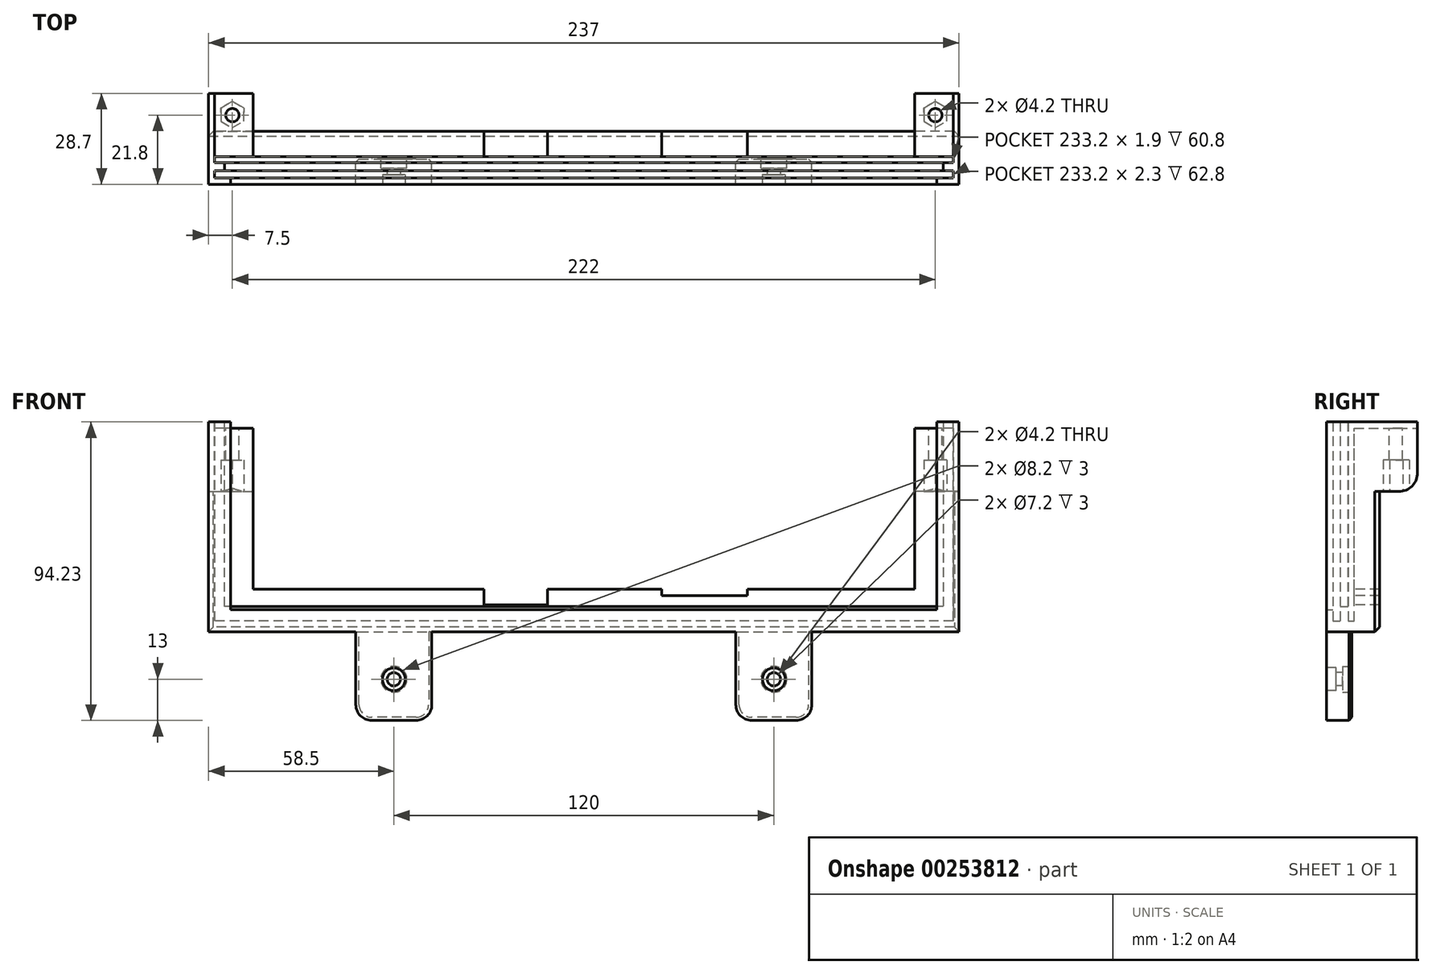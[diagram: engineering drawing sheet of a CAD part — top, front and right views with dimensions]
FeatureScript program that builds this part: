
annotation { "Feature Type Name" : "Feature", "Feature Type Description" : "" }
export const myFeature = defineFeature(function(context is Context, id is Id, definition is map)
    precondition{}
    {
        {
            var Q0;
            Q0=qCreatedBy(makeId("Front.planeOp"),FACE);
            var sketch = newSketch(context, id + "F0", { "sketchPlane" : qUnion([Q0])});
            skLineSegment(sketch, "E0", {"start": v(118.5, 0) * mm, "end": v(118.5, 66.23) * mm});
            skLineSegment(sketch, "E1", {"start": v(118.5, 66.23) * mm, "end": v(104.5, 66.23) * mm});
            skLineSegment(sketch, "E2", {"start": v(104.5, 66.23) * mm, "end": v(104.5, 13.43) * mm});
            skLineSegment(sketch, "E3", {"start": v(104.5, 13.43) * mm, "end": v(-104.5, 13.43) * mm});
            skLineSegment(sketch, "E4", {"start": v(-104.5, 13.43) * mm, "end": v(-104.5, 66.23) * mm});
            skLineSegment(sketch, "E5", {"start": v(-104.5, 66.23) * mm, "end": v(-118.5, 66.23) * mm});
            skLineSegment(sketch, "E6", {"start": v(-118.5, 66.23) * mm, "end": v(-118.5, 0) * mm});
            skLineSegment(sketch, "E7", {"start": v(-118.5, 0) * mm, "end": v(118.5, 0) * mm});
            skSolve(sketch);
        }
        {
            var Q0;
            Q0=makeQuery(id+"F0.imprint","IMPRINT",FACE,{"disambiguationData":[TD([[makeQuery(id+"F0.imprint","IMPRINT",EDGE,{"derivedFrom":sQuery(id+"F0.wireOp",EDGE,"E0")}),1.0]])]});
            extrude(context, id + "F1", {"entities" : qUnion([Q0]), "depth" : 8 * mm, "offsetDistance" : 25 * mm});
        }
        {
            var Q0;
            Q0=makeQuery(id+"F1.opExtrude","CAP_FACE",FACE,{"disambiguationData":[OSD([sQuery(id+"F0.wireOp",EDGE,"E0"),sQuery(id+"F0.wireOp",EDGE,"E1"),sQuery(id+"F0.wireOp",EDGE,"E2"),sQuery(id+"F0.wireOp",EDGE,"E3"),sQuery(id+"F0.wireOp",EDGE,"E4"),sQuery(id+"F0.wireOp",EDGE,"E5"),sQuery(id+"F0.wireOp",EDGE,"E6"),sQuery(id+"F0.wireOp",EDGE,"E7")])],"isStart":false});
            var sketch = newSketch(context, id + "F2", { "sketchPlane" : qUnion([Q0])});
            skLineSegment(sketch, "E8", {"start": v(-118.5, 66.23) * mm, "end": v(-118.5, 0) * mm});
            skLineSegment(sketch, "E9", {"start": v(-118.5, 0) * mm, "end": v(118.5, 0) * mm});
            skLineSegment(sketch, "E10", {"start": v(118.5, 0) * mm, "end": v(118.5, 66.23) * mm});
            skLineSegment(sketch, "E11", {"start": v(118.5, 66.23) * mm, "end": v(116.6, 66.23) * mm});
            skLineSegment(sketch, "E12", {"start": v(116.6, 66.23) * mm, "end": v(116.6, 3.43) * mm});
            skLineSegment(sketch, "E13", {"start": v(116.6, 3.43) * mm, "end": v(-116.6, 3.43) * mm});
            skLineSegment(sketch, "E14", {"start": v(-116.6, 3.43) * mm, "end": v(-116.6, 66.23) * mm});
            skLineSegment(sketch, "E15", {"start": v(-116.6, 66.23) * mm, "end": v(-118.5, 66.23) * mm});
            skSolve(sketch);
        }
        {
            var Q0;
            Q0 = qSketchRegion(id + "F2", true);
            extrude(context, id + "F3", {"entities" : qUnion([Q0]), "operationType" : NewBodyOperationType.ADD, "offsetDistance" : 25 * mm, "depth" : 1.9 * mm});
        }
        {
            var Q0;
            Q0=makeQuery(id+"F3.opExtrude","CAP_FACE",FACE,{"disambiguationData":[OSD([sQuery(id+"F2.wireOp",EDGE,"E8"),sQuery(id+"F2.wireOp",EDGE,"E9"),sQuery(id+"F2.wireOp",EDGE,"E10"),sQuery(id+"F2.wireOp",EDGE,"E11"),sQuery(id+"F2.wireOp",EDGE,"E12"),sQuery(id+"F2.wireOp",EDGE,"E13"),sQuery(id+"F2.wireOp",EDGE,"E14"),sQuery(id+"F2.wireOp",EDGE,"E15")])],"isStart":false});
            var sketch = newSketch(context, id + "F4", { "sketchPlane" : qUnion([Q0])});
            skLineSegment(sketch, "E16", {"start": v(-118.5, 66.23) * mm, "end": v(-118.5, 0) * mm});
            skLineSegment(sketch, "E17", {"start": v(-118.5, 0) * mm, "end": v(118.5, 0) * mm});
            skLineSegment(sketch, "E18", {"start": v(118.5, 0) * mm, "end": v(118.5, 66.23) * mm});
            skLineSegment(sketch, "E19", {"start": v(118.5, 66.23) * mm, "end": v(113.5, 66.23) * mm});
            skLineSegment(sketch, "E20", {"start": v(-113.5, 8) * mm, "end": v(-113.5, 66.23) * mm});
            skLineSegment(sketch, "E21", {"start": v(-113.5, 66.23) * mm, "end": v(-118.5, 66.23) * mm});
            skLineSegment(sketch, "E22", {"start": v(113.5, 66.23) * mm, "end": v(113.5, 8) * mm});
            skLineSegment(sketch, "E23", {"start": v(113.5, 8) * mm, "end": v(-113.5, 8) * mm});
            skSolve(sketch);
        }
        {
            var Q0;
            Q0 = qSketchRegion(id + "F4", true);
            extrude(context, id + "F5", {"entities" : qUnion([Q0]), "operationType" : NewBodyOperationType.ADD, "offsetDistance" : 25 * mm, "depth" : 2.5 * mm});
        }
        {
            var Q0;
            Q0=makeQuery(id+"F5.opExtrude","CAP_FACE",FACE,{"disambiguationData":[OSD([sQuery(id+"F4.wireOp",EDGE,"E16"),sQuery(id+"F4.wireOp",EDGE,"E17"),sQuery(id+"F4.wireOp",EDGE,"E18"),sQuery(id+"F4.wireOp",EDGE,"E19"),sQuery(id+"F4.wireOp",EDGE,"Wqc7Pmu5-h7pA-NfiT-lCzg-tGP6uvwJ4WZ4"),sQuery(id+"F4.wireOp",EDGE,"H4PolKqh-P5Vf-ZCvA-0sDl-Pb70Bhz4lyF4"),sQuery(id+"F4.wireOp",EDGE,"E20"),sQuery(id+"F4.wireOp",EDGE,"E21")])],"isStart":false});
            var sketch = newSketch(context, id + "F6", { "sketchPlane" : qUnion([Q0])});
            skLineSegment(sketch, "E24", {"start": v(-118.5, 66.23) * mm, "end": v(-116.6, 66.23) * mm});
            skLineSegment(sketch, "E25", {"start": v(-116.6, 66.23) * mm, "end": v(-116.6, 3.43) * mm});
            skLineSegment(sketch, "E26", {"start": v(-116.6, 3.43) * mm, "end": v(116.6, 3.43) * mm});
            skLineSegment(sketch, "E27", {"start": v(116.6, 3.43) * mm, "end": v(116.6, 66.23) * mm});
            skLineSegment(sketch, "E28", {"start": v(116.6, 66.23) * mm, "end": v(118.5, 66.23) * mm});
            skLineSegment(sketch, "E29", {"start": v(118.5, 66.23) * mm, "end": v(118.5, 0) * mm});
            skLineSegment(sketch, "E30", {"start": v(118.5, 0) * mm, "end": v(-118.5, 0) * mm});
            skLineSegment(sketch, "E31", {"start": v(-118.5, 0) * mm, "end": v(-118.5, 66.23) * mm});
            skSolve(sketch);
        }
        {
            var Q0;
            Q0 = qSketchRegion(id + "F6", true);
            extrude(context, id + "F7", {"entities" : qUnion([Q0]), "operationType" : NewBodyOperationType.ADD, "offsetDistance" : 25 * mm, "depth" : 2.3 * mm});
        }
        {
            var Q0;
            Q0=makeQuery(id+"F7.opExtrude","CAP_FACE",FACE,{"disambiguationData":[OSD([sQuery(id+"F6.wireOp",EDGE,"E24"),sQuery(id+"F6.wireOp",EDGE,"E25"),sQuery(id+"F6.wireOp",EDGE,"E26"),sQuery(id+"F6.wireOp",EDGE,"E27"),sQuery(id+"F6.wireOp",EDGE,"E28"),sQuery(id+"F6.wireOp",EDGE,"E29"),sQuery(id+"F6.wireOp",EDGE,"E30"),sQuery(id+"F6.wireOp",EDGE,"E31")])],"isStart":false});
            var sketch = newSketch(context, id + "F8", { "sketchPlane" : qUnion([Q0])});
            skLineSegment(sketch, "E32", {"start": v(-118.5, 66.23) * mm, "end": v(-118.5, 0) * mm});
            skLineSegment(sketch, "E33", {"start": v(-118.5, 0) * mm, "end": v(118.5, 0) * mm});
            skLineSegment(sketch, "E34", {"start": v(118.5, 0) * mm, "end": v(118.5, 66.23) * mm});
            skLineSegment(sketch, "E35", {"start": v(118.5, 66.23) * mm, "end": v(111.5, 66.23) * mm});
            skLineSegment(sketch, "E36", {"start": v(111.5, 66.23) * mm, "end": v(111.5, 7) * mm});
            skLineSegment(sketch, "E37", {"start": v(111.5, 7) * mm, "end": v(-111.5, 7) * mm});
            skLineSegment(sketch, "E38", {"start": v(-111.5, 7) * mm, "end": v(-111.5, 66.23) * mm});
            skLineSegment(sketch, "E39", {"start": v(-111.5, 66.23) * mm, "end": v(-118.5, 66.23) * mm});
            skSolve(sketch);
        }
        {
            var Q0;
            Q0=makeQuery(id+"F1.opExtrude","CAP_FACE",FACE,{"disambiguationData":[OSD([sQuery(id+"F0.wireOp",EDGE,"E0"),sQuery(id+"F0.wireOp",EDGE,"E1"),sQuery(id+"F0.wireOp",EDGE,"E2"),sQuery(id+"F0.wireOp",EDGE,"E3"),sQuery(id+"F0.wireOp",EDGE,"E4"),sQuery(id+"F0.wireOp",EDGE,"E5"),sQuery(id+"F0.wireOp",EDGE,"E6"),sQuery(id+"F0.wireOp",EDGE,"E7")])],"isStart":true});
            var sketch = newSketch(context, id + "F9", { "sketchPlane" : qUnion([Q0])});
            skLineSegment(sketch, "E40.bottom", {"start": v(118.5, 66.23) * mm, "end": v(104.5, 66.23) * mm});
            skLineSegment(sketch, "E40.top", {"start": v(118.5, 44.23) * mm, "end": v(104.5, 44.23) * mm});
            skLineSegment(sketch, "E40.left", {"start": v(118.5, 66.23) * mm, "end": v(118.5, 44.23) * mm});
            skLineSegment(sketch, "E40.right", {"start": v(104.5, 66.23) * mm, "end": v(104.5, 44.23) * mm});
            skLineSegment(sketch, "E41.bottom", {"start": v(-118.5, 66.23) * mm, "end": v(-104.5, 66.23) * mm});
            skLineSegment(sketch, "E41.top", {"start": v(-118.5, 44.23) * mm, "end": v(-104.5, 44.23) * mm});
            skLineSegment(sketch, "E41.left", {"start": v(-118.5, 66.23) * mm, "end": v(-118.5, 44.23) * mm});
            skLineSegment(sketch, "E41.right", {"start": v(-104.5, 66.23) * mm, "end": v(-104.5, 44.23) * mm});
            skSolve(sketch);
        }
        {
            var Q0;
            Q0 = qSketchRegion(id + "F9", true);
            extrude(context, id + "F10", {"entities" : qUnion([Q0]), "operationType" : NewBodyOperationType.ADD, "depth" : 12 * mm, "offsetDistance" : 25 * mm});
        }
        {
            var Q0;
            Q0 = qSketchRegion(id + "F8", true);
            extrude(context, id + "F11", {"entities" : qUnion([Q0]), "operationType" : NewBodyOperationType.ADD, "depth" : 2 * mm});
        }
        {
            var Q0;
            Q0=makeQuery(id+"F11.boolean.opBoolean","MERGE",FACE,{"derivedFrom":[makeQuery(id+"F7.boolean.opBoolean","MERGE",FACE,{"derivedFrom":[makeQuery(id+"F5.boolean.opBoolean","MERGE",FACE,{"derivedFrom":[makeQuery(id+"F3.boolean.opBoolean","MERGE",FACE,{"derivedFrom":[makeQuery(id+"F1.opExtrude","SWEPT_FACE",FACE,{"disambiguationData":[OSD([sQuery(id+"F0.wireOp",EDGE,"E5")])]}),makeQuery(id+"F3.opExtrude","SWEPT_FACE",FACE,{"disambiguationData":[OSD([sQuery(id+"F2.wireOp",EDGE,"E15")])]})]}),makeQuery(id+"F5.opExtrude","SWEPT_FACE",FACE,{"disambiguationData":[OSD([sQuery(id+"F4.wireOp",EDGE,"E21")])]})]}),makeQuery(id+"F7.opExtrude","SWEPT_FACE",FACE,{"disambiguationData":[OSD([sQuery(id+"F6.wireOp",EDGE,"E24")])]})]}),makeQuery(id+"F11.opExtrude","SWEPT_FACE",FACE,{"disambiguationData":[OSD([sQuery(id+"F8.wireOp",EDGE,"E39")])]})]});
            var sketch = newSketch(context, id + "F12", { "sketchPlane" : qUnion([Q0])});
            skLineSegment(sketch, "E42.bottom", {"start": v(-116.6, -8) * mm, "end": v(-104.5, -8) * mm});
            skLineSegment(sketch, "E42.top", {"start": v(-116.6, 12) * mm, "end": v(-104.5, 12) * mm});
            skLineSegment(sketch, "E42.left", {"start": v(-116.6, -8) * mm, "end": v(-116.6, 12) * mm});
            skLineSegment(sketch, "E42.right", {"start": v(-104.5, -8) * mm, "end": v(-104.5, 12) * mm});
            skSolve(sketch);
        }
        {
            var Q0;
            Q0=makeQuery(id+"F11.boolean.opBoolean","MERGE",FACE,{"derivedFrom":[makeQuery(id+"F7.boolean.opBoolean","MERGE",FACE,{"derivedFrom":[makeQuery(id+"F5.boolean.opBoolean","MERGE",FACE,{"derivedFrom":[makeQuery(id+"F3.boolean.opBoolean","MERGE",FACE,{"derivedFrom":[makeQuery(id+"F1.opExtrude","SWEPT_FACE",FACE,{"disambiguationData":[OSD([sQuery(id+"F0.wireOp",EDGE,"E1")])]}),makeQuery(id+"F3.opExtrude","SWEPT_FACE",FACE,{"disambiguationData":[OSD([sQuery(id+"F2.wireOp",EDGE,"E11")])]})]}),makeQuery(id+"F5.opExtrude","SWEPT_FACE",FACE,{"disambiguationData":[OSD([sQuery(id+"F4.wireOp",EDGE,"E19")])]})]}),makeQuery(id+"F7.opExtrude","SWEPT_FACE",FACE,{"disambiguationData":[OSD([sQuery(id+"F6.wireOp",EDGE,"E28")])]})]}),makeQuery(id+"F11.opExtrude","SWEPT_FACE",FACE,{"disambiguationData":[OSD([sQuery(id+"F8.wireOp",EDGE,"E35")])]})]});
            var sketch = newSketch(context, id + "F13", { "sketchPlane" : qUnion([Q0])});
            skLineSegment(sketch, "E43.bottom", {"start": v(116.6, -8) * mm, "end": v(104.5, -8) * mm});
            skLineSegment(sketch, "E43.top", {"start": v(116.6, 12) * mm, "end": v(104.5, 12) * mm});
            skLineSegment(sketch, "E43.left", {"start": v(116.6, -8) * mm, "end": v(116.6, 12) * mm});
            skLineSegment(sketch, "E43.right", {"start": v(104.5, -8) * mm, "end": v(104.5, 12) * mm});
            skSolve(sketch);
        }
        {
            var Q0;
            Q0 = qSketchRegion(id + "F12", true);
            var Q1;
            Q1 = qSketchRegion(id + "F13", true);
            extrude(context, id + "F14", {"entities" : qUnion([Q0, Q1]), "operationType" : NewBodyOperationType.REMOVE, "oppositeDirection" : true, "depth" : 2 * mm});
        }
        {
            var Q0;
            Q0=makeQuery(id+"F10.opExtrude","SWEPT_FACE",FACE,{"disambiguationData":[OSD([sQuery(id+"F9.wireOp",EDGE,"E41.top")])]});
            var sketch = newSketch(context, id + "F15", { "sketchPlane" : qUnion([Q0])});
            skCircle(sketch, "E44.cCircle", {"center": v(111, -5.3) * mm, "radius": 3.6 * mm, "construction": true});
            skLineSegment(sketch, "E44.0", {"start": v(107.4, -3.22) * mm, "end": v(111, -1.14) * mm});
            skLineSegment(sketch, "E44.1", {"start": v(111, -1.14) * mm, "end": v(114.6, -3.22) * mm});
            skLineSegment(sketch, "E44.2", {"start": v(114.6, -3.22) * mm, "end": v(114.6, -7.38) * mm});
            skLineSegment(sketch, "E44.3", {"start": v(114.6, -7.38) * mm, "end": v(111, -9.46) * mm});
            skLineSegment(sketch, "E44.4", {"start": v(111, -9.46) * mm, "end": v(107.4, -7.38) * mm});
            skLineSegment(sketch, "E44.5", {"start": v(107.4, -7.38) * mm, "end": v(107.4, -3.22) * mm});
            skPoint(sketch, "E44.0.midPoint", {"position": v(109.2, -2.18) * mm});
            skSolve(sketch);
        }
        {
            var Q0;
            Q0=makeQuery(id+"F10.opExtrude","SWEPT_FACE",FACE,{"disambiguationData":[OSD([sQuery(id+"F9.wireOp",EDGE,"E40.top")])]});
            var sketch = newSketch(context, id + "F16", { "sketchPlane" : qUnion([Q0])});
            skCircle(sketch, "E45.cCircle", {"center": v(-111, -5.3) * mm, "radius": 3.6 * mm, "construction": true});
            skLineSegment(sketch, "E45.0", {"start": v(-107.4, -3.22) * mm, "end": v(-107.4, -7.38) * mm});
            skLineSegment(sketch, "E45.1", {"start": v(-107.4, -7.38) * mm, "end": v(-111, -9.46) * mm});
            skLineSegment(sketch, "E45.2", {"start": v(-111, -9.46) * mm, "end": v(-114.6, -7.38) * mm});
            skLineSegment(sketch, "E45.3", {"start": v(-114.6, -7.38) * mm, "end": v(-114.6, -3.22) * mm});
            skLineSegment(sketch, "E45.4", {"start": v(-114.6, -3.22) * mm, "end": v(-111, -1.14) * mm});
            skLineSegment(sketch, "E45.5", {"start": v(-111, -1.14) * mm, "end": v(-107.4, -3.22) * mm});
            skPoint(sketch, "E45.0.midPoint", {"position": v(-107.4, -5.3) * mm});
            skSolve(sketch);
        }
        {
            var Q0;
            {var subQ0=sQuery(id+"F9.wireOp",EDGE,"E40.top");Q0=makeQuery(id+"F10.boolean.opBoolean","SPLIT",EDGE,{"disambiguationData":[topologyDisambiguationEdgeConnected([makeQuery(id+"F1.opExtrude","CAP_FACE",FACE,{"disambiguationData":[OSD([sQuery(id+"F0.wireOp",EDGE,"E0"),sQuery(id+"F0.wireOp",EDGE,"E1"),sQuery(id+"F0.wireOp",EDGE,"E2"),sQuery(id+"F0.wireOp",EDGE,"E3"),sQuery(id+"F0.wireOp",EDGE,"E4"),sQuery(id+"F0.wireOp",EDGE,"E5"),sQuery(id+"F0.wireOp",EDGE,"E6"),sQuery(id+"F0.wireOp",EDGE,"E7")])],"isStart":true})])],"derivedFrom":makeQuery(id+"F10.opExtrude","CAP_EDGE",EDGE,{"disambiguationData":[OSD([subQ0])],"isStart":true})});}
            var Q1;
            Q1=makeQuery(id+"F10.opExtrude","CAP_EDGE",EDGE,{"disambiguationData":[OSD([sQuery(id+"F9.wireOp",EDGE,"E40.top")])],"isStart":false});
            var Q2;
            Q2=makeQuery(id+"F10.opExtrude","CAP_EDGE",EDGE,{"disambiguationData":[OSD([sQuery(id+"F9.wireOp",EDGE,"zH6vjrLi-htQf-ZEOU-owel-cehFYXmzGVBA.top")])],"isStart":true});
            var Q3;
            Q3=makeQuery(id+"F10.opExtrude","CAP_EDGE",EDGE,{"disambiguationData":[OSD([sQuery(id+"F9.wireOp",EDGE,"zH6vjrLi-htQf-ZEOU-owel-cehFYXmzGVBA.bottom")])],"isStart":false});
            fillet(context, id + "F17", {"entities" : qUnion([Q0, Q1, Q2, Q3]), "radius" : 6 * mm, "tangentPropagation" : true, "allowEdgeOverflow" : false});
        }
        {
            var Q0;
            {var subQ0=sQuery(id+"F9.wireOp",EDGE,"E41.top");Q0=makeQuery(id+"F10.boolean.opBoolean","SPLIT",EDGE,{"disambiguationData":[topologyDisambiguationEdgeConnected([makeQuery(id+"F1.opExtrude","CAP_FACE",FACE,{"disambiguationData":[OSD([sQuery(id+"F0.wireOp",EDGE,"E0"),sQuery(id+"F0.wireOp",EDGE,"E1"),sQuery(id+"F0.wireOp",EDGE,"E2"),sQuery(id+"F0.wireOp",EDGE,"E3"),sQuery(id+"F0.wireOp",EDGE,"E4"),sQuery(id+"F0.wireOp",EDGE,"E5"),sQuery(id+"F0.wireOp",EDGE,"E6"),sQuery(id+"F0.wireOp",EDGE,"E7")])],"isStart":true})])],"derivedFrom":makeQuery(id+"F10.opExtrude","CAP_EDGE",EDGE,{"disambiguationData":[OSD([subQ0])],"isStart":true})});}
            var Q1;
            Q1=makeQuery(id+"F10.opExtrude","CAP_EDGE",EDGE,{"disambiguationData":[OSD([sQuery(id+"F9.wireOp",EDGE,"E41.top")])],"isStart":false});
            var Q2;
            Q2=makeQuery(id+"F10.opExtrude","CAP_EDGE",EDGE,{"disambiguationData":[OSD([sQuery(id+"F9.wireOp",EDGE,"rV4yrqaR-FLz1-uUMA-ZUjG-8FGM3lznCrda.top")])],"isStart":true});
            var Q3;
            Q3=makeQuery(id+"F10.opExtrude","CAP_EDGE",EDGE,{"disambiguationData":[OSD([sQuery(id+"F9.wireOp",EDGE,"rV4yrqaR-FLz1-uUMA-ZUjG-8FGM3lznCrda.bottom")])],"isStart":false});
            fillet(context, id + "F18", {"entities" : qUnion([Q0, Q1, Q2, Q3]), "radius" : 6 * mm, "tangentPropagation" : true, "allowEdgeOverflow" : false});
        }
        {
            var Q0;
            Q0 = qSketchRegion(id + "F15", true);
            var Q1;
            Q1 = qSketchRegion(id + "F16", true);
            extrude(context, id + "F19", {"entities" : qUnion([Q0, Q1]), "operationType" : NewBodyOperationType.REMOVE, "oppositeDirection" : true, "depth" : 10 * mm});
        }
        {
            var Q0;
            Q0 = qSketchRegion(id + "F15", true);
            var Q1;
            Q1 = qSketchRegion(id + "F16", true);
            extrude(context, id + "F20", {"entities" : qUnion([Q0, Q1]), "operationType" : NewBodyOperationType.REMOVE, "depth" : 25 * mm});
        }
        {
            var Q0;
            Q0=makeQuery(id+"F14.boolean.opBoolean","COPY",FACE,{"derivedFrom":makeQuery(id+"F14.opExtrude","CAP_FACE",FACE,{"disambiguationData":[OSD([sQuery(id+"F12.wireOp",EDGE,"E42.bottom"),sQuery(id+"F12.wireOp",EDGE,"E42.top"),sQuery(id+"F12.wireOp",EDGE,"E42.left"),sQuery(id+"F12.wireOp",EDGE,"E42.right")])],"isStart":false})});
            var sketch = newSketch(context, id + "F21", { "sketchPlane" : qUnion([Q0])});
            skCircle(sketch, "E46", {"center": v(-111, 5.1) * mm, "radius": 2.1 * mm});
            skSolve(sketch);
        }
        {
            var Q0;
            Q0=makeQuery(id+"F14.boolean.opBoolean","COPY",FACE,{"derivedFrom":makeQuery(id+"F14.opExtrude","CAP_FACE",FACE,{"disambiguationData":[OSD([sQuery(id+"F13.wireOp",EDGE,"E43.bottom"),sQuery(id+"F13.wireOp",EDGE,"E43.top"),sQuery(id+"F13.wireOp",EDGE,"E43.left"),sQuery(id+"F13.wireOp",EDGE,"E43.right")])],"isStart":false})});
            var sketch = newSketch(context, id + "F22", { "sketchPlane" : qUnion([Q0])});
            skCircle(sketch, "E47", {"center": v(111, 5.1) * mm, "radius": 2.1 * mm});
            skSolve(sketch);
        }
        {
            var Q0;
            Q0 = qSketchRegion(id + "F22", true);
            var Q1;
            Q1 = qSketchRegion(id + "F21", true);
            extrude(context, id + "F23", {"entities" : qUnion([Q0, Q1]), "operationType" : NewBodyOperationType.REMOVE, "endBound" : BoundingType.UP_TO_NEXT, "oppositeDirection" : true, "depth" : 25 * mm, "offsetDistance" : 25 * mm});
        }
        {
            var Q0;
            Q0=makeQuery(id+"F1.opExtrude","CAP_EDGE",EDGE,{"disambiguationData":[OSD([sQuery(id+"F0.wireOp",EDGE,"E0")])],"isStart":true});
            var Q1;
            Q1=makeQuery(id+"F17.opFillet","BLEND_EDGE",EDGE,{"blendedFrom":[makeQuery(id+"F10.boolean.opBoolean","COPY",EDGE,{"derivedFrom":makeQuery(id+"F10.opExtrude","CAP_EDGE",EDGE,{"disambiguationData":[OSD([sQuery(id+"F9.wireOp",EDGE,"GcGkKbpC-YmWN-ICau-n4Ke-VAg4k9SfYREq")])],"isStart":true})}),makeQuery(id+"F11.boolean.opBoolean","MERGE",FACE,{"derivedFrom":[makeQuery(id+"F7.boolean.opBoolean","MERGE",FACE,{"derivedFrom":[makeQuery(id+"F5.boolean.opBoolean","MERGE",FACE,{"derivedFrom":[makeQuery(id+"F3.boolean.opBoolean","MERGE",FACE,{"derivedFrom":[makeQuery(id+"F1.opExtrude","SWEPT_FACE",FACE,{"disambiguationData":[OSD([sQuery(id+"F0.wireOp",EDGE,"E0")])]}),makeQuery(id+"F3.opExtrude","SWEPT_FACE",FACE,{"disambiguationData":[OSD([sQuery(id+"F2.wireOp",EDGE,"E10")])]})]}),makeQuery(id+"F5.opExtrude","SWEPT_FACE",FACE,{"disambiguationData":[OSD([sQuery(id+"F4.wireOp",EDGE,"E18")])]})]}),makeQuery(id+"F7.opExtrude","SWEPT_FACE",FACE,{"disambiguationData":[OSD([sQuery(id+"F6.wireOp",EDGE,"E29")])]})]}),makeQuery(id+"F11.opExtrude","SWEPT_FACE",FACE,{"disambiguationData":[OSD([sQuery(id+"F8.wireOp",EDGE,"E34")])]})]})],"blendedInto":[makeQuery(id+"F11.boolean.opBoolean","MERGE",FACE,{"derivedFrom":[makeQuery(id+"F7.boolean.opBoolean","MERGE",FACE,{"derivedFrom":[makeQuery(id+"F5.boolean.opBoolean","MERGE",FACE,{"derivedFrom":[makeQuery(id+"F3.boolean.opBoolean","MERGE",FACE,{"derivedFrom":[makeQuery(id+"F1.opExtrude","SWEPT_FACE",FACE,{"disambiguationData":[OSD([sQuery(id+"F0.wireOp",EDGE,"E0")])]}),makeQuery(id+"F3.opExtrude","SWEPT_FACE",FACE,{"disambiguationData":[OSD([sQuery(id+"F2.wireOp",EDGE,"E10")])]})]}),makeQuery(id+"F5.opExtrude","SWEPT_FACE",FACE,{"disambiguationData":[OSD([sQuery(id+"F4.wireOp",EDGE,"E18")])]})]}),makeQuery(id+"F7.opExtrude","SWEPT_FACE",FACE,{"disambiguationData":[OSD([sQuery(id+"F6.wireOp",EDGE,"E29")])]})]}),makeQuery(id+"F11.opExtrude","SWEPT_FACE",FACE,{"disambiguationData":[OSD([sQuery(id+"F8.wireOp",EDGE,"E34")])]})]})]});
            var Q2;
            Q2=makeQuery(id+"F17.opFillet","BLEND_EDGE",EDGE,{"blendedFrom":[makeQuery(id+"F10.boolean.opBoolean","COPY",EDGE,{"derivedFrom":makeQuery(id+"F10.opExtrude","CAP_EDGE",EDGE,{"disambiguationData":[OSD([sQuery(id+"F9.wireOp",EDGE,"GcGkKbpC-YmWN-ICau-n4Ke-VAg4k9SfYREq")])],"isStart":false})}),makeQuery(id+"F11.boolean.opBoolean","MERGE",FACE,{"derivedFrom":[makeQuery(id+"F7.boolean.opBoolean","MERGE",FACE,{"derivedFrom":[makeQuery(id+"F5.boolean.opBoolean","MERGE",FACE,{"derivedFrom":[makeQuery(id+"F3.boolean.opBoolean","MERGE",FACE,{"derivedFrom":[makeQuery(id+"F1.opExtrude","SWEPT_FACE",FACE,{"disambiguationData":[OSD([sQuery(id+"F0.wireOp",EDGE,"E0")])]}),makeQuery(id+"F3.opExtrude","SWEPT_FACE",FACE,{"disambiguationData":[OSD([sQuery(id+"F2.wireOp",EDGE,"E10")])]})]}),makeQuery(id+"F5.opExtrude","SWEPT_FACE",FACE,{"disambiguationData":[OSD([sQuery(id+"F4.wireOp",EDGE,"E18")])]})]}),makeQuery(id+"F7.opExtrude","SWEPT_FACE",FACE,{"disambiguationData":[OSD([sQuery(id+"F6.wireOp",EDGE,"E29")])]})]}),makeQuery(id+"F11.opExtrude","SWEPT_FACE",FACE,{"disambiguationData":[OSD([sQuery(id+"F8.wireOp",EDGE,"E34")])]})]})],"blendedInto":[makeQuery(id+"F11.boolean.opBoolean","MERGE",FACE,{"derivedFrom":[makeQuery(id+"F7.boolean.opBoolean","MERGE",FACE,{"derivedFrom":[makeQuery(id+"F5.boolean.opBoolean","MERGE",FACE,{"derivedFrom":[makeQuery(id+"F3.boolean.opBoolean","MERGE",FACE,{"derivedFrom":[makeQuery(id+"F1.opExtrude","SWEPT_FACE",FACE,{"disambiguationData":[OSD([sQuery(id+"F0.wireOp",EDGE,"E0")])]}),makeQuery(id+"F3.opExtrude","SWEPT_FACE",FACE,{"disambiguationData":[OSD([sQuery(id+"F2.wireOp",EDGE,"E10")])]})]}),makeQuery(id+"F5.opExtrude","SWEPT_FACE",FACE,{"disambiguationData":[OSD([sQuery(id+"F4.wireOp",EDGE,"E18")])]})]}),makeQuery(id+"F7.opExtrude","SWEPT_FACE",FACE,{"disambiguationData":[OSD([sQuery(id+"F6.wireOp",EDGE,"E29")])]})]}),makeQuery(id+"F11.opExtrude","SWEPT_FACE",FACE,{"disambiguationData":[OSD([sQuery(id+"F8.wireOp",EDGE,"E34")])]})]})]});
            var Q3;
            Q3=makeQuery(id+"F10.boolean.opBoolean","COPY",EDGE,{"derivedFrom":makeQuery(id+"F10.opExtrude","CAP_EDGE",EDGE,{"disambiguationData":[OSD([sQuery(id+"F9.wireOp",EDGE,"H9YxvoyA-mwdu-Ozs1-Mgqu-f7LAvOGyu2lw")])],"isStart":false})});
            var Q4;
            Q4=makeQuery(id+"F10.boolean.opBoolean","COPY",EDGE,{"derivedFrom":makeQuery(id+"F10.opExtrude","CAP_EDGE",EDGE,{"disambiguationData":[OSD([sQuery(id+"F9.wireOp",EDGE,"rf6zfMRu-Qe2T-Zb9I-k2tc-n19xOsOlgDaL")])],"isStart":false})});
            var Q5;
            Q5=makeQuery(id+"F10.boolean.opBoolean","COPY",EDGE,{"derivedFrom":makeQuery(id+"F10.opExtrude","CAP_EDGE",EDGE,{"disambiguationData":[OSD([sQuery(id+"F9.wireOp",EDGE,"47vZZXop-T4Wf-DfnT-CCxK-A6Yf87ua8k3M")])],"isStart":false})});
            var Q6;
            Q6=makeQuery(id+"F18.opFillet","BLEND_EDGE",EDGE,{"blendedFrom":[makeQuery(id+"F10.boolean.opBoolean","COPY",EDGE,{"derivedFrom":makeQuery(id+"F10.opExtrude","CAP_EDGE",EDGE,{"disambiguationData":[OSD([sQuery(id+"F9.wireOp",EDGE,"PPJEcUq0-yMRA-Zqzy-vXhF-8VfT6uxw4NmP")])],"isStart":false})}),makeQuery(id+"F11.boolean.opBoolean","MERGE",FACE,{"derivedFrom":[makeQuery(id+"F7.boolean.opBoolean","MERGE",FACE,{"derivedFrom":[makeQuery(id+"F5.boolean.opBoolean","MERGE",FACE,{"derivedFrom":[makeQuery(id+"F3.boolean.opBoolean","MERGE",FACE,{"derivedFrom":[makeQuery(id+"F1.opExtrude","SWEPT_FACE",FACE,{"disambiguationData":[OSD([sQuery(id+"F0.wireOp",EDGE,"E6")])]}),makeQuery(id+"F3.opExtrude","SWEPT_FACE",FACE,{"disambiguationData":[OSD([sQuery(id+"F2.wireOp",EDGE,"E8")])]})]}),makeQuery(id+"F5.opExtrude","SWEPT_FACE",FACE,{"disambiguationData":[OSD([sQuery(id+"F4.wireOp",EDGE,"E16")])]})]}),makeQuery(id+"F7.opExtrude","SWEPT_FACE",FACE,{"disambiguationData":[OSD([sQuery(id+"F6.wireOp",EDGE,"E31")])]})]}),makeQuery(id+"F11.opExtrude","SWEPT_FACE",FACE,{"disambiguationData":[OSD([sQuery(id+"F8.wireOp",EDGE,"E32")])]})]})],"blendedInto":[makeQuery(id+"F11.boolean.opBoolean","MERGE",FACE,{"derivedFrom":[makeQuery(id+"F7.boolean.opBoolean","MERGE",FACE,{"derivedFrom":[makeQuery(id+"F5.boolean.opBoolean","MERGE",FACE,{"derivedFrom":[makeQuery(id+"F3.boolean.opBoolean","MERGE",FACE,{"derivedFrom":[makeQuery(id+"F1.opExtrude","SWEPT_FACE",FACE,{"disambiguationData":[OSD([sQuery(id+"F0.wireOp",EDGE,"E6")])]}),makeQuery(id+"F3.opExtrude","SWEPT_FACE",FACE,{"disambiguationData":[OSD([sQuery(id+"F2.wireOp",EDGE,"E8")])]})]}),makeQuery(id+"F5.opExtrude","SWEPT_FACE",FACE,{"disambiguationData":[OSD([sQuery(id+"F4.wireOp",EDGE,"E16")])]})]}),makeQuery(id+"F7.opExtrude","SWEPT_FACE",FACE,{"disambiguationData":[OSD([sQuery(id+"F6.wireOp",EDGE,"E31")])]})]}),makeQuery(id+"F11.opExtrude","SWEPT_FACE",FACE,{"disambiguationData":[OSD([sQuery(id+"F8.wireOp",EDGE,"E32")])]})]})]});
            var Q7;
            Q7=makeQuery(id+"F18.opFillet","BLEND_EDGE",EDGE,{"blendedFrom":[makeQuery(id+"F10.boolean.opBoolean","COPY",EDGE,{"derivedFrom":makeQuery(id+"F10.opExtrude","CAP_EDGE",EDGE,{"disambiguationData":[OSD([sQuery(id+"F9.wireOp",EDGE,"PPJEcUq0-yMRA-Zqzy-vXhF-8VfT6uxw4NmP")])],"isStart":true})}),makeQuery(id+"F11.boolean.opBoolean","MERGE",FACE,{"derivedFrom":[makeQuery(id+"F7.boolean.opBoolean","MERGE",FACE,{"derivedFrom":[makeQuery(id+"F5.boolean.opBoolean","MERGE",FACE,{"derivedFrom":[makeQuery(id+"F3.boolean.opBoolean","MERGE",FACE,{"derivedFrom":[makeQuery(id+"F1.opExtrude","SWEPT_FACE",FACE,{"disambiguationData":[OSD([sQuery(id+"F0.wireOp",EDGE,"E6")])]}),makeQuery(id+"F3.opExtrude","SWEPT_FACE",FACE,{"disambiguationData":[OSD([sQuery(id+"F2.wireOp",EDGE,"E8")])]})]}),makeQuery(id+"F5.opExtrude","SWEPT_FACE",FACE,{"disambiguationData":[OSD([sQuery(id+"F4.wireOp",EDGE,"E16")])]})]}),makeQuery(id+"F7.opExtrude","SWEPT_FACE",FACE,{"disambiguationData":[OSD([sQuery(id+"F6.wireOp",EDGE,"E31")])]})]}),makeQuery(id+"F11.opExtrude","SWEPT_FACE",FACE,{"disambiguationData":[OSD([sQuery(id+"F8.wireOp",EDGE,"E32")])]})]})],"blendedInto":[makeQuery(id+"F11.boolean.opBoolean","MERGE",FACE,{"derivedFrom":[makeQuery(id+"F7.boolean.opBoolean","MERGE",FACE,{"derivedFrom":[makeQuery(id+"F5.boolean.opBoolean","MERGE",FACE,{"derivedFrom":[makeQuery(id+"F3.boolean.opBoolean","MERGE",FACE,{"derivedFrom":[makeQuery(id+"F1.opExtrude","SWEPT_FACE",FACE,{"disambiguationData":[OSD([sQuery(id+"F0.wireOp",EDGE,"E6")])]}),makeQuery(id+"F3.opExtrude","SWEPT_FACE",FACE,{"disambiguationData":[OSD([sQuery(id+"F2.wireOp",EDGE,"E8")])]})]}),makeQuery(id+"F5.opExtrude","SWEPT_FACE",FACE,{"disambiguationData":[OSD([sQuery(id+"F4.wireOp",EDGE,"E16")])]})]}),makeQuery(id+"F7.opExtrude","SWEPT_FACE",FACE,{"disambiguationData":[OSD([sQuery(id+"F6.wireOp",EDGE,"E31")])]})]}),makeQuery(id+"F11.opExtrude","SWEPT_FACE",FACE,{"disambiguationData":[OSD([sQuery(id+"F8.wireOp",EDGE,"E32")])]})]})]});
            var Q8;
            Q8=makeQuery(id+"F1.opExtrude","CAP_EDGE",EDGE,{"disambiguationData":[OSD([sQuery(id+"F0.wireOp",EDGE,"E6")])],"isStart":true});
            var Q9;
            Q9=makeQuery(id+"F10.opExtrude","CAP_EDGE",EDGE,{"disambiguationData":[OSD([sQuery(id+"F9.wireOp",EDGE,"rV4yrqaR-FLz1-uUMA-ZUjG-8FGM3lznCrda.left")])],"isStart":false});
            var Q10;
            Q10=makeQuery(id+"F10.opExtrude","CAP_EDGE",EDGE,{"disambiguationData":[OSD([sQuery(id+"F9.wireOp",EDGE,"zH6vjrLi-htQf-ZEOU-owel-cehFYXmzGVBA.left")])],"isStart":false});
            var Q11;
            Q11=makeQuery(id+"F1.opExtrude","CAP_EDGE",EDGE,{"disambiguationData":[OSD([sQuery(id+"F0.wireOp",EDGE,"E7")])],"isStart":true});
            chamfer(context, id + "F24", {"entities" : qUnion([Q0, Q1, Q2, Q3, Q4, Q5, Q6, Q7, Q8, Q9, Q10, Q11]), "width" : 1.5 * mm, "tangentPropagation" : true});
        }
        {
            var Q0;
            Q0=makeQuery(id+"F11.boolean.opBoolean","MERGE",FACE,{"derivedFrom":[makeQuery(id+"F7.boolean.opBoolean","MERGE",FACE,{"derivedFrom":[makeQuery(id+"F5.boolean.opBoolean","MERGE",FACE,{"derivedFrom":[makeQuery(id+"F3.boolean.opBoolean","MERGE",FACE,{"derivedFrom":[makeQuery(id+"F1.opExtrude","SWEPT_FACE",FACE,{"disambiguationData":[OSD([sQuery(id+"F0.wireOp",EDGE,"E7")])]}),makeQuery(id+"F3.opExtrude","SWEPT_FACE",FACE,{"disambiguationData":[OSD([sQuery(id+"F2.wireOp",EDGE,"E9")])]})]}),makeQuery(id+"F5.opExtrude","SWEPT_FACE",FACE,{"disambiguationData":[OSD([sQuery(id+"F4.wireOp",EDGE,"E17")])]})]}),makeQuery(id+"F7.opExtrude","SWEPT_FACE",FACE,{"disambiguationData":[OSD([sQuery(id+"F6.wireOp",EDGE,"E30")])]})]}),makeQuery(id+"F11.opExtrude","SWEPT_FACE",FACE,{"disambiguationData":[OSD([sQuery(id+"F8.wireOp",EDGE,"E33")])]})]});
            var sketch = newSketch(context, id + "F25", { "sketchPlane" : qUnion([Q0])});
            skLineSegment(sketch, "E48.bottom", {"start": v(-72, 16.7) * mm, "end": v(-48, 16.7) * mm});
            skLineSegment(sketch, "E48.top", {"start": v(-72, 8.7) * mm, "end": v(-48, 8.7) * mm});
            skLineSegment(sketch, "E48.left", {"start": v(-72, 16.7) * mm, "end": v(-72, 8.7) * mm});
            skLineSegment(sketch, "E48.right", {"start": v(-48, 16.7) * mm, "end": v(-48, 8.7) * mm});
            skLineSegment(sketch, "E49.bottom", {"start": v(48, 16.7) * mm, "end": v(72, 16.7) * mm});
            skLineSegment(sketch, "E49.top", {"start": v(48, 8.7) * mm, "end": v(72, 8.7) * mm});
            skLineSegment(sketch, "E49.left", {"start": v(48, 16.7) * mm, "end": v(48, 8.7) * mm});
            skLineSegment(sketch, "E49.right", {"start": v(72, 16.7) * mm, "end": v(72, 8.7) * mm});
            skSolve(sketch);
        }
        {
            var Q0;
            Q0 = qSketchRegion(id + "F25", true);
            extrude(context, id + "F26", {"entities" : qUnion([Q0]), "operationType" : NewBodyOperationType.ADD, "offsetDistance" : 25 * mm, "depth" : 28 * mm});
        }
        {
            var Q0;
            Q0=makeQuery(id+"F26.opExtrude","SWEPT_FACE",FACE,{"disambiguationData":[OSD([sQuery(id+"F25.wireOp",EDGE,"E48.top")])]});
            var sketch = newSketch(context, id + "F27", { "sketchPlane" : qUnion([Q0])});
            skCircle(sketch, "E50", {"center": v(60, -15) * mm, "radius": 4.1 * mm});
            skSolve(sketch);
        }
        {
            var Q0;
            Q0=makeQuery(id+"F26.opExtrude","SWEPT_FACE",FACE,{"disambiguationData":[OSD([sQuery(id+"F25.wireOp",EDGE,"E49.top")])]});
            var sketch = newSketch(context, id + "F28", { "sketchPlane" : qUnion([Q0])});
            skCircle(sketch, "E51", {"center": v(-60, -15) * mm, "radius": 4.1 * mm});
            skSolve(sketch);
        }
        {
            var Q0;
            Q0 = qSketchRegion(id + "F28", true);
            var Q1;
            Q1 = qSketchRegion(id + "F27", true);
            extrude(context, id + "F29", {"entities" : qUnion([Q0, Q1]), "operationType" : NewBodyOperationType.REMOVE, "oppositeDirection" : true, "depth" : 3 * mm});
        }
        {
            var Q0;
            Q0=makeQuery(id+"F26.boolean.opBoolean","MERGE",FACE,{"derivedFrom":[makeQuery(id+"F11.opExtrude","CAP_FACE",FACE,{"disambiguationData":[OSD([sQuery(id+"F8.wireOp",EDGE,"E32"),sQuery(id+"F8.wireOp",EDGE,"E33"),sQuery(id+"F8.wireOp",EDGE,"E34"),sQuery(id+"F8.wireOp",EDGE,"E35"),sQuery(id+"F8.wireOp",EDGE,"E36"),sQuery(id+"F8.wireOp",EDGE,"E37"),sQuery(id+"F8.wireOp",EDGE,"E38"),sQuery(id+"F8.wireOp",EDGE,"E39")])],"isStart":false}),makeQuery(id+"F26.opExtrude","SWEPT_FACE",FACE,{"disambiguationData":[OSD([sQuery(id+"F25.wireOp",EDGE,"E48.bottom")])]}),makeQuery(id+"F26.opExtrude","SWEPT_FACE",FACE,{"disambiguationData":[OSD([sQuery(id+"F25.wireOp",EDGE,"E49.bottom")])]})]});
            var sketch = newSketch(context, id + "F30", { "sketchPlane" : qUnion([Q0])});
            skCircle(sketch, "E52", {"center": v(-60, -15) * mm, "radius": 2.1 * mm});
            skCircle(sketch, "E53", {"center": v(60, -15) * mm, "radius": 2.1 * mm});
            skSolve(sketch);
        }
        {
            var Q0;
            Q0 = qSketchRegion(id + "F30", true);
            extrude(context, id + "F31", {"entities" : qUnion([Q0]), "operationType" : NewBodyOperationType.REMOVE, "endBound" : BoundingType.THROUGH_ALL, "oppositeDirection" : true, "depth" : 25 * mm});
        }
        {
            var Q0;
            Q0=makeQuery(id+"F26.boolean.opBoolean","MERGE",FACE,{"derivedFrom":[makeQuery(id+"F11.opExtrude","CAP_FACE",FACE,{"disambiguationData":[OSD([sQuery(id+"F8.wireOp",EDGE,"E32"),sQuery(id+"F8.wireOp",EDGE,"E33"),sQuery(id+"F8.wireOp",EDGE,"E34"),sQuery(id+"F8.wireOp",EDGE,"E35"),sQuery(id+"F8.wireOp",EDGE,"E36"),sQuery(id+"F8.wireOp",EDGE,"E37"),sQuery(id+"F8.wireOp",EDGE,"E38"),sQuery(id+"F8.wireOp",EDGE,"E39")])],"isStart":false}),makeQuery(id+"F26.opExtrude","SWEPT_FACE",FACE,{"disambiguationData":[OSD([sQuery(id+"F25.wireOp",EDGE,"E48.bottom")])]}),makeQuery(id+"F26.opExtrude","SWEPT_FACE",FACE,{"disambiguationData":[OSD([sQuery(id+"F25.wireOp",EDGE,"E49.bottom")])]})]});
            var sketch = newSketch(context, id + "F32", { "sketchPlane" : qUnion([Q0])});
            skCircle(sketch, "E54", {"center": v(-60, -15) * mm, "radius": 3.6 * mm});
            skCircle(sketch, "E55", {"center": v(60, -15) * mm, "radius": 3.6 * mm});
            skSolve(sketch);
        }
        {
            var Q0;
            Q0 = qSketchRegion(id + "F32", true);
            extrude(context, id + "F33", {"entities" : qUnion([Q0]), "operationType" : NewBodyOperationType.REMOVE, "oppositeDirection" : true, "depth" : 3 * mm});
        }
        {
            var Q0;
            Q0=makeQuery(id+"F26.opExtrude","CAP_EDGE",EDGE,{"disambiguationData":[OSD([sQuery(id+"F25.wireOp",EDGE,"E48.left")])],"isStart":false});
            var Q1;
            Q1=makeQuery(id+"F26.opExtrude","CAP_EDGE",EDGE,{"disambiguationData":[OSD([sQuery(id+"F25.wireOp",EDGE,"E48.right")])],"isStart":false});
            var Q2;
            Q2=makeQuery(id+"F26.opExtrude","CAP_EDGE",EDGE,{"disambiguationData":[OSD([sQuery(id+"F25.wireOp",EDGE,"E49.left")])],"isStart":false});
            var Q3;
            Q3=makeQuery(id+"F26.opExtrude","CAP_EDGE",EDGE,{"disambiguationData":[OSD([sQuery(id+"F25.wireOp",EDGE,"E49.right")])],"isStart":false});
            fillet(context, id + "F34", {"entities" : qUnion([Q0, Q1, Q2, Q3]), "radius" : 5 * mm, "tangentPropagation" : true, "allowEdgeOverflow" : false});
        }
        {
            var Q0;
            Q0=makeQuery(id+"F1.opExtrude","SWEPT_FACE",FACE,{"disambiguationData":[OSD([sQuery(id+"F0.wireOp",EDGE,"E3")])]});
            var sketch = newSketch(context, id + "F35", { "sketchPlane" : qUnion([Q0])});
            skLineSegment(sketch, "E56.bottom", {"start": v(-31.5, 0) * mm, "end": v(-11.5, 0) * mm});
            skLineSegment(sketch, "E56.top", {"start": v(-31.5, -8) * mm, "end": v(-11.5, -8) * mm});
            skLineSegment(sketch, "E56.left", {"start": v(-31.5, 0) * mm, "end": v(-31.5, -8) * mm});
            skLineSegment(sketch, "E56.right", {"start": v(-11.5, 0) * mm, "end": v(-11.5, -8) * mm});
            skSolve(sketch);
        }
        {
            var Q0;
            Q0 = qSketchRegion(id + "F35", true);
            extrude(context, id + "F36", {"entities" : qUnion([Q0]), "operationType" : NewBodyOperationType.REMOVE, "oppositeDirection" : true, "depth" : 5 * mm, "offsetDistance" : 25 * mm});
        }
        {
            var Q0;
            Q0=makeQuery(id+"F26.opExtrude","SWEPT_EDGE",EDGE,{"disambiguationData":[OSD([sQuery(id+"F25.wireOp",EDGE,"E48.top"),sQuery(id+"F25.wireOp",EDGE,"E48.left")])]});
            var Q1;
            Q1=makeQuery(id+"F26.opExtrude","SWEPT_EDGE",EDGE,{"disambiguationData":[OSD([sQuery(id+"F25.wireOp",EDGE,"E49.top"),sQuery(id+"F25.wireOp",EDGE,"E49.right")])]});
            var Q2;
            Q2=makeQuery(id+"F26.opExtrude","SWEPT_EDGE",EDGE,{"disambiguationData":[OSD([sQuery(id+"F25.wireOp",EDGE,"E49.top"),sQuery(id+"F25.wireOp",EDGE,"E49.left")])]});
            var Q3;
            Q3=makeQuery(id+"F26.opExtrude","SWEPT_EDGE",EDGE,{"disambiguationData":[OSD([sQuery(id+"F25.wireOp",EDGE,"E48.top"),sQuery(id+"F25.wireOp",EDGE,"E48.right")])]});
            chamfer(context, id + "F37", {"entities" : qUnion([Q0, Q1, Q2, Q3]), "width" : 1 * mm, "tangentPropagation" : true});
        }
        {
            var Q0;
            {var subQ4=sQuery(id+"F0.wireOp",EDGE,"E3");var subQ5=sQuery(id+"F0.wireOp",EDGE,"E2");Q0=makeQuery(id+"F36.boolean.opBoolean","SPLIT",FACE,{"disambiguationData":[TD([makeQuery(id+"F1.opExtrude","SWEPT_FACE",FACE,{"disambiguationData":[OSD([subQ5])]})])],"derivedFrom":makeQuery(id+"F1.opExtrude","SWEPT_FACE",FACE,{"disambiguationData":[OSD([subQ4])]})});}
            var sketch = newSketch(context, id + "F38", { "sketchPlane" : qUnion([Q0])});
            skLineSegment(sketch, "E57.bottom", {"start": v(24.6, 0) * mm, "end": v(51.6, 0) * mm});
            skLineSegment(sketch, "E57.top", {"start": v(24.6, -8) * mm, "end": v(51.6, -8) * mm});
            skLineSegment(sketch, "E57.left", {"start": v(24.6, 0) * mm, "end": v(24.6, -8) * mm});
            skLineSegment(sketch, "E57.right", {"start": v(51.6, 0) * mm, "end": v(51.6, -8) * mm});
            skSolve(sketch);
        }
        {
            var Q0;
            Q0 = qSketchRegion(id + "F38", true);
            extrude(context, id + "F39", {"entities" : qUnion([Q0]), "operationType" : NewBodyOperationType.REMOVE, "oppositeDirection" : true, "depth" : 2 * mm, "offsetDistance" : 25 * mm});
        }
    });
